FCSTD DOCUMENT  (FreeCAD 0.16R5097 (Git))
Label: Base section
License: All rights reserved
LicenseURL: http://en.wikipedia.org/wiki/All_rights_reserved
objects: Part::Part2DObjectPython×50, App::Annotation×8, App::FeaturePython×3, Part::Feature×1, App::DocumentObjectGroup×1
note: 51 computed .brp shape members not serialized (recipe doc carries the construction recipe); baked Part::Feature solids carry a one-line shape summary decoded from their .brp

FEATURE [Part::Part2DObjectPython] Rectangle  # Draft 2D object (typed FeaturePython)
  ChamferSize = 0
  FilletRadius = 0
  Height = 2438.4
  Length = 152.4
  MakeFace = true
  Placement = pos=(8.9e-11,-4058.4,0) rot=(0,0,1;0rad)
FEATURE [Part::Part2DObjectPython] Rectangle001  # Draft 2D object (typed FeaturePython)
  ChamferSize = 0
  FilletRadius = 0
  Height = 152.4
  Length = 4876.8
  MakeFace = true
  Placement = pos=(-152.4,-1680.96,0) rot=(0,0,1;0.197396rad)
  Support = -> Rectangle
FEATURE [Part::Part2DObjectPython] Rectangle002  # Draft 2D object (typed FeaturePython)
  ChamferSize = 0
  FilletRadius = 0
  Height = 152.4
  Length = 50.8
  MakeFace = true
  Placement = pos=(-152.4,-1680.96,0) rot=(0,0,1;0.197396rad)
FEATURE [Part::Part2DObjectPython] Rectangle003  # Draft 2D object (typed FeaturePython)
  ChamferSize = 0
  FilletRadius = 0
  Height = 152.4
  Length = 50.8
  MakeFace = true
  Placement = pos=(26.9286,-1541.48,0) rot=(0,0,1;1.76819rad)
FEATURE [Part::Part2DObjectPython] Rectangle004  # Draft 2D object (typed FeaturePython)
  ChamferSize = 0
  FilletRadius = 0
  Height = 152.4
  Length = 50.8
  MakeFace = true
  Placement = pos=(152.4,-1670.8,0) rot=(0,0,1;1.5708rad)
FEATURE [Part::Part2DObjectPython] Rectangle005  # Draft 2D object (typed FeaturePython)
  ChamferSize = 0
  FilletRadius = 0
  Height = 152.4
  Length = 50.8
  MakeFace = true
  Placement = pos=(152.4,-1670.8,0) rot=(0,0,1;3.14159rad)
FEATURE [Part::Part2DObjectPython] Rectangle006  # Draft 2D object (typed FeaturePython)
  ChamferSize = 0
  FilletRadius = 0
  Height = 152.4
  Length = 50.8
  MakeFace = true
  Placement = pos=(4579.88,-734.504,0) rot=(0,0,1;0.197396rad)
FEATURE [Part::Part2DObjectPython] Rectangle007  # Draft 2D object (typed FeaturePython)
  ChamferSize = 0
  FilletRadius = 0
  Height = 152.4
  Length = 50.8
  MakeFace = true
  Placement = pos=(4579.88,-734.504,0) rot=(0,0,1;1.76819rad)
FEATURE [Part::Part2DObjectPython] Rectangle008  # Draft 2D object (typed FeaturePython)
  ChamferSize = 0
  FilletRadius = 0
  Height = 152.4
  Length = 50.8
  MakeFace = true
  Placement = pos=(152.4,-4058.4,0) rot=(0,0,1;1.5708rad)
FEATURE [Part::Part2DObjectPython] Rectangle009  # Draft 2D object (typed FeaturePython)
  ChamferSize = 0
  FilletRadius = 0
  Height = 152.4
  Length = 50.8
  MakeFace = true
  Placement = pos=(152.4,-3855.2,0) rot=(0,0,1;3.14159rad)
FEATURE [Part::Part2DObjectPython] Rectangle010  # Draft 2D object (typed FeaturePython)
  ChamferSize = 0
  FilletRadius = 0
  Height = 5000
  Length = 522.38
  MakeFace = true
  Placement = pos=(4629.7,-4209.2,0) rot=(0,0,1;0rad)
FEATURE [Part::Part2DObjectPython] Line  # Draft 2D object (typed FeaturePython)
  ChamferSize = 0
  Closed = false
  End = (101.6,-1260.93,0)
  FilletRadius = 0
  Length = 647.743
  MakeFace = true
  Placement = pos=(-50.8,-1908.67,0) rot=(0,0,1;0rad)
  Points = (2) [(152.4,1.15278e-10,0),(152.4,647.743,0)]
  Start = (101.6,-1908.67,0)
FEATURE [Part::Part2DObjectPython] Line001  # Draft 2D object (typed FeaturePython)
  ChamferSize = 0
  Closed = false
  End = (50.8,-1260.93,0)
  FilletRadius = 0
  Length = 647.743
  MakeFace = true
  Placement = pos=(-101.6,-1908.67,0) rot=(0,0,1;0rad)
  Points = (2) [(152.4,1.15278e-10,0),(152.4,647.743,0)]
  Start = (50.8,-1908.67,0)
FEATURE [Part::Part2DObjectPython] Rectangle011  # Draft 2D object (typed FeaturePython)
  ChamferSize = 0
  FilletRadius = 0
  Height = 125
  Length = 12.7
  MakeFace = true
  Placement = pos=(-20.3985,-1667.51,0) rot=(0,0,1;1.76819rad)
FEATURE [Part::Part2DObjectPython] Rectangle012  # Draft 2D object (typed FeaturePython)
  ChamferSize = 0
  FilletRadius = 0
  Height = 152.4
  Length = 50.8
  MakeFace = true
  Placement = pos=(4629.7,-735.134,0) rot=(0,0,1;3.14159rad)
FEATURE [Part::Part2DObjectPython] Line002  # Draft 2D object (typed FeaturePython)
  ChamferSize = 0
  Closed = false
  End = (5428.22,-836.734,0)
  FilletRadius = 0
  Length = 1050.78
  MakeFace = true
  Placement = pos=(-92.5719,-1606.18,0) rot=(0,0,1;0rad)
  Points = (2) [(4470.01,769.444,0),(5520.79,769.444,0)]
  Start = (4377.44,-836.734,0)
FEATURE [Part::Part2DObjectPython] Line003  # Draft 2D object (typed FeaturePython)
  ChamferSize = 0
  Closed = false
  End = (5428.22,-785.934,0)
  FilletRadius = 0
  Length = 1050.78
  MakeFace = true
  Placement = pos=(-92.5719,-1555.38,0) rot=(0,0,1;0rad)
  Points = (2) [(4470.01,769.444,0),(5520.79,769.444,0)]
  Start = (4377.44,-785.934,0)
FEATURE [App::FeaturePython] Dimension  # Draft dimension (typed FeaturePython)
  Dimline = (3460.82,-387.376,0)
  Direction = (0,0,0)
  Distance = 4876.8
  End = (4599.81,-575.1,0)
  Normal = (0,0,1)
  Start = (-182.288,-1531.52,0)
FEATURE [Part::Part2DObjectPython] Rectangle013  # Draft 2D object (typed FeaturePython)
  ChamferSize = 0
  FilletRadius = 0
  Height = 100
  Length = 200
  MakeFace = true
  Placement = pos=(-23.8,-4209.2,0) rot=(0,0,1;0rad)
FEATURE [Part::Part2DObjectPython] Rectangle014  # Draft 2D object (typed FeaturePython)
  ChamferSize = 0
  FilletRadius = 0
  Height = -778.465
  Length = 723.456
  MakeFace = true
  Placement = pos=(-285.528,-4209.2,0) rot=(0,0,1;0rad)
FEATURE [Part::Part2DObjectPython] Rectangle015  # Draft 2D object (typed FeaturePython)
  ChamferSize = 0
  FilletRadius = 0
  Height = -778.465
  Length = 723.456
  MakeFace = true
  Placement = pos=(4529.16,-4209.2,0) rot=(0,0,1;0rad)
FEATURE [Part::Part2DObjectPython] Line004  # Draft 2D object (typed FeaturePython)
  ChamferSize = 0
  Closed = false
  End = (4529.16,-4209.2,0)
  FilletRadius = 0
  Length = 4091.23
  MakeFace = true
  Placement = pos=(0,-101.6,0) rot=(0,0,1;0rad)
  Points = (2) [(437.928,-4107.6,0),(4529.16,-4107.6,0)]
  Start = (437.928,-4209.2,0)
FEATURE [Part::Part2DObjectPython] Rectangle016  # Draft 2D object (typed FeaturePython)
  ChamferSize = 0
  FilletRadius = 0
  Height = 152.4
  Length = 50.8
  MakeFace = true
  Placement = pos=(152.4,-4109.2,0) rot=(0,0,1;1.5708rad)
FEATURE [Part::Part2DObjectPython] Line005  # Draft 2D object (typed FeaturePython)
  ChamferSize = 0
  Closed = false
  End = (76.2,-3764.74,0)
  FilletRadius = 0
  Length = 647.743
  MakeFace = true
  Placement = pos=(-76.2,-4412.49,0) rot=(0,0,1;0rad)
  Points = (2) [(152.4,1.15278e-10,0),(152.4,647.743,0)]
  Start = (76.2,-4412.49,0)
FEATURE [Part::Feature] Polyline  label="Person"
  Placement = pos=(2144.04,-4210.4,0) rot=(0,0,1;0rad)
  shape: bbox 1200 x 1818 x 2e-07 mm, 0 faces, 0 solids (baked)
FEATURE [App::FeaturePython] Dimension001  # Draft dimension (typed FeaturePython)
  Dimline = (-514.519,-2392.01,0)
  Direction = (0,0,0)
  Distance = 2438.4
  End = (8.9e-11,-1620,0)
  Normal = (0,0,1)
  Start = (8.9e-11,-4058.4,0)
FEATURE [App::Annotation] Text
  LabelText = 16' Roof panel | 20% slope
  Position = (-2666.11,-30.1774,0)
FEATURE [Part::Part2DObjectPython] DWire  # Draft 2D object (typed FeaturePython)
  ChamferSize = 0
  Closed = false
  End = (-1566.37,17.1876,0)
  FilletRadius = 0
  Length = 3282.33
  MakeFace = true
  Placement = pos=(0,-400.8,0) rot=(0,0,1;0rad)
  Points = (3) [(1362.29,-901.705,0),(-923.076,417.988,0),(-1566.37,417.988,0)]
  Start = (1362.29,-1302.5,0)
FEATURE [App::Annotation] Text001
  LabelText = 8' Wall panel
  Position = (-2497.25,-2807.56,0)
FEATURE [Part::Part2DObjectPython] Line006  # Draft 2D object (typed FeaturePython)
  ChamferSize = 0
  Closed = false
  End = (-1581.02,-2769.61,0)
  FilletRadius = 0
  Length = 1658.15
  MakeFace = true
  Points = (2) [(77.136,-2769.61,0),(-1581.02,-2769.61,0)]
  Start = (77.136,-2769.61,0)
FEATURE [App::Annotation] Text002
  LabelText = Base lumber fixed to wall
  Position = (-2517.74,-3766.66,0)
FEATURE [Part::Part2DObjectPython] DWire001  # Draft 2D object (typed FeaturePython)
  ChamferSize = 0
  Closed = false
  End = (-826.195,-3718.63,0)
  FilletRadius = 0
  Length = 962.724
  MakeFace = true
  Placement = pos=(0,-400.8,0) rot=(0,0,1;0rad)
  Points = (3) [(40.5394,-3686.9,-3.63798e-12),(-620.962,-3317.83,0),(-826.195,-3317.83,0)]
  Start = (40.5394,-4087.7,-4e-12)
FEATURE [App::Annotation] Text004
  LabelText = Brick wall
  Position = (-2518.73,-4197.79,0)
FEATURE [Part::Part2DObjectPython] Line008  # Draft 2D object (typed FeaturePython)
  ChamferSize = 0
  Closed = false
  End = (-1752.02,-4159.49,0)
  FilletRadius = 0
  Length = 1796.36
  MakeFace = true
  Placement = pos=(0,-121.402,0) rot=(0,0,1;0rad)
  Points = (2) [(44.3355,-4038.09,0),(-1752.02,-4038.09,0)]
  Start = (44.3355,-4159.49,0)
FEATURE [App::Annotation] Text005
  LabelText = Dent in roof panel
  Position = (-2571.01,-1065.68,0)
FEATURE [Part::Part2DObjectPython] DWire002  # Draft 2D object (typed FeaturePython)
  ChamferSize = 0
  Closed = false
  End = (-1335.08,-1042.56,0)
  FilletRadius = 0
  Length = 1571.43
  MakeFace = true
  Placement = pos=(0,-400.8,0) rot=(0,0,1;0rad)
  Points = (3) [(71.6956,-1211.56,0),(-831.87,-641.759,0),(-1335.08,-641.759,0)]
  Start = (71.6956,-1612.36,0)
FEATURE [App::Annotation] Text006
  LabelText = Finishing board
  Position = (-2546.96,-2098.36,0)
FEATURE [Part::Part2DObjectPython] DWire003  # Draft 2D object (typed FeaturePython)
  ChamferSize = 0
  Closed = false
  End = (-1462.47,-2094.45,0)
  FilletRadius = 0
  Length = 1481.11
  MakeFace = true
  Placement = pos=(0,-400.8,0) rot=(0,0,1;0rad)
  Points = (3) [(-60.1521,-1322.04,0),(-897.069,-1693.65,0),(-1462.47,-1693.65,0)]
  Start = (-60.1521,-1722.84,0)
FEATURE [Part::Part2DObjectPython] DWire004  # Draft 2D object (typed FeaturePython)
  ChamferSize = 0
  Closed = true
  End = (8.9e-11,-1249.68,0)
  FilletRadius = 0
  Length = 10085.9
  MakeFace = true
  Points = (7) [(-152.4,-1280.16,0),(-182.288,-1130.72,0),(4599.81,-174.3,0),(4629.7,-323.741,0),(152.4,-1219.2,0),(8.90452e-11,-1219.2,0),(8.90282e-11,-1249.68,0)]
  Start = (-152.4,-1280.16,0)
FEATURE [Part::Part2DObjectPython] Rectangle018  # Draft 2D object (typed FeaturePython)
  ChamferSize = 0
  FilletRadius = 0
  Height = 11.1125
  Length = 4876.8
  MakeFace = true
  Placement = pos=(-182.288,-1531.52,0) rot=(0,0,1;0.197396rad)
FEATURE [Part::Part2DObjectPython] Rectangle019  # Draft 2D object (typed FeaturePython)
  ChamferSize = 0
  FilletRadius = 0
  Height = 2438.4
  Length = 11.1125
  MakeFace = true
  Placement = pos=(-11.1125,-4058.4,0) rot=(0,0,1;0rad)
FEATURE [Part::Part2DObjectPython] DWire005  # Draft 2D object (typed FeaturePython)
  ChamferSize = 0
  Closed = false
  End = (-161.67,-1541.05,0)
  FilletRadius = 0
  Length = 87.7772
  MakeFace = true
  Placement = pos=(0,-400.8,0) rot=(0,0,1;0rad)
  Points = (4) [(-171.767,-1106.66,0),(-195.649,-1111.32,0),(-189.436,-1145.88,0),(-161.67,-1140.25,0)]
  Start = (-171.767,-1507.46,0)
FEATURE [Part::Part2DObjectPython] DWire006  # Draft 2D object (typed FeaturePython)
  ChamferSize = 0
  Closed = false
  End = (-34.7813,-1631.15,0)
  FilletRadius = 0
  Length = 68.1851
  MakeFace = true
  Placement = pos=(0,-400.8,0) rot=(0,0,1;0rad)
  Points = (3) [(-15.5742,-1279.33,0),(-15.5742,-1230.35,0),(-34.7813,-1230.35,0)]
  Start = (-15.5742,-1680.13,0)
FEATURE [Part::Part2DObjectPython] DWire007  # Draft 2D object (typed FeaturePython)
  ChamferSize = 0
  Closed = false
  End = (4595.7,-348.454,0)
  FilletRadius = 0
  Length = 332.263
  MakeFace = true
  Placement = pos=(0,-400.8,0) rot=(0,0,1;0rad)
  Points = (3) [(4450.38,-162.586,0),(4595.7,-131.26,0),(4595.7,52.3464,0)]
  Start = (4450.38,-563.386,0)
FEATURE [Part::Part2DObjectPython] Line009  # Draft 2D object (typed FeaturePython)
  ChamferSize = 0
  Closed = false
  End = (4807.89,-446.588,0)
  FilletRadius = 0
  Length = 291.238
  MakeFace = true
  Placement = pos=(0,-400.8,0) rot=(0,0,1;0rad)
  Points = (2) [(4516.66,-45.7882,0),(4807.89,-45.7882,0)]
  Start = (4516.66,-446.588,0)
FEATURE [App::Annotation] Text007
  LabelText = Flashing
  Position = (2432.2,257.338,0)
FEATURE [Part::Part2DObjectPython] DWire008  # Draft 2D object (typed FeaturePython)
  ChamferSize = 0
  Closed = false
  End = (3052.14,288.618,0)
  FilletRadius = 0
  Length = 1750.97
  MakeFace = true
  Placement = pos=(0,-400.8,0) rot=(0,0,1;0rad)
  Points = (3) [(4554.15,-95.885,0),(3440.06,689.418,0),(3052.14,689.418,0)]
  Start = (4554.15,-496.685,0)
FEATURE [Part::Part2DObjectPython] Circle  # Draft 2D object (typed FeaturePython)
  FirstAngle = 0
  LastAngle = 0
  MakeFace = true
  Placement = pos=(76.1173,-4055.83,0) rot=(0,1,0;3.14159rad)
  Radius = 331.844
FEATURE [Part::Part2DObjectPython] Circle001  # Draft 2D object (typed FeaturePython)
  FirstAngle = 0
  LastAngle = 0
  MakeFace = true
  Placement = pos=(8.9e-11,-1650.48,0) rot=(0,0,1;0rad)
  Radius = 358.624
FEATURE [Part::Part2DObjectPython] Circle002  # Draft 2D object (typed FeaturePython)
  FirstAngle = 0
  LastAngle = 0
  MakeFace = true
  Placement = pos=(4629.7,-724.541,0) rot=(0,0,1;0rad)
  Radius = 463.13
FEATURE [Part::Part2DObjectPython] Rectangle020  # Draft 2D object (typed FeaturePython)
  ChamferSize = 0
  FilletRadius = 0
  Height = 152.4
  Length = 50.8
  MakeFace = true
  Placement = pos=(4578.9,-748.114,0) rot=(0,0,1;3.14159rad)
FEATURE [Part::Part2DObjectPython] Line011  # Draft 2D object (typed FeaturePython)
  ChamferSize = 0
  Closed = false
  End = (4619.47,-1133.79,0)
  FilletRadius = 0
  Length = 756.941
  MakeFace = true
  Placement = pos=(1239.31,-159.34,0) rot=(0,0,1;0rad)
  Points = (2) [(3231.71,-232.207,0),(3380.16,-974.448,0)]
  Start = (4471.02,-391.547,0)
FEATURE [Part::Part2DObjectPython] DWire009  # Draft 2D object (typed FeaturePython)
  ChamferSize = 0
  Closed = false
  End = (-33.5428,-4124.98,0)
  FilletRadius = 0
  Length = 268.403
  MakeFace = true
  Points = (4) [(186.183,-4123.64,0),(186.183,-4099.97,0),(-33.5428,-4099.97,0),(-33.5428,-4124.98,0)]
  Start = (186.183,-4123.64,0)
FEATURE [App::Annotation] Text008
  LabelText = Flashing
  Position = (-2516.03,-3991.32,0)
FEATURE [Part::Part2DObjectPython] DWire010  # Draft 2D object (typed FeaturePython)
  ChamferSize = 0
  Closed = false
  End = (-1898.25,-3978.59,0)
  FilletRadius = 0
  Length = 1882.13
  MakeFace = true
  Points = (3) [(-50.282,-4110.41,0),(-287.507,-3978.59,0),(-1898.25,-3978.59,0)]
  Start = (-50.282,-4110.41,0)
FEATURE [App::DocumentObjectGroup] Group  label="Section"
  Group = -> [Rectangle,Rectangle001,Rectangle002,Rectangle003,Rectangle004,Rectangle005,Rectangle006,Rectangle007,Rectangle008,Rectangle009,Rectangle010,Line,Line001,Rectangle011,Rectangle012,Line002,Line003,Dimension,Rectangle013,Rectangle014,Rectangle015,Line004,Rectangle016,Line005,Polyline,Dimension001,Text,DWire,Text001,Line006,Text002,DWire001,Text004,Line008,Text005,DWire002,Text006,DWire003,DWire004,+16 more]
FEATURE [App::FeaturePython] Dimension002  # Draft dimension (typed FeaturePython)
  Dimline = (700.265,-2646.59,0)
  Direction = (0,0,0)
  Distance = 2589.31
  End = (152.4,-1620,0)
  Normal = (0,0,1)
  Start = (176.2,-4209.2,0)
FEATURE [Part::Part2DObjectPython] Rectangle021  # Draft 2D object (typed FeaturePython)
  ChamferSize = 0
  FilletRadius = 0
  Height = 2438.4
  Length = 1219.2
  MakeFace = false
  Placement = pos=(152.4,-4058.4,0) rot=(0,0,1;0rad)
FEATURE [Part::Part2DObjectPython] Rectangle022  # Draft 2D object (typed FeaturePython)
  ChamferSize = 0
  FilletRadius = 0
  Height = 2438.4
  Length = 1219.2
  MakeFace = false
  Placement = pos=(1371.6,-4058.4,0) rot=(0,0,1;0rad)
FEATURE [Part::Part2DObjectPython] Rectangle023  # Draft 2D object (typed FeaturePython)
  ChamferSize = 0
  FilletRadius = 0
  Height = 2438.4
  Length = 1219.2
  MakeFace = false
  Placement = pos=(2590.8,-4058.4,0) rot=(0,0,1;0rad)
FEATURE [Part::Part2DObjectPython] Rectangle024  # Draft 2D object (typed FeaturePython)
  ChamferSize = 0
  FilletRadius = 0
  Height = 2438.4
  Length = 820
  MakeFace = false
  Placement = pos=(3810,-4058.4,0) rot=(0,0,1;0rad)
FEATURE [Part::Part2DObjectPython] Line012  # Draft 2D object (typed FeaturePython)
  ChamferSize = 0
  Closed = false
  End = (282.609,-1747,0)
  FilletRadius = 0
  Length = 263.855
  MakeFace = true
  Placement = pos=(0,-2.65601,0) rot=(0,0,1;0rad)
  Points = (2) [(18.754,-1744.34,0),(282.609,-1744.34,0)]
  Start = (18.754,-1747,0)
FEATURE [Part::Part2DObjectPython] Line013  # Draft 2D object (typed FeaturePython)
  ChamferSize = 0
  Closed = false
  End = (282.609,-3931.4,0)
  FilletRadius = 0
  Length = 263.855
  MakeFace = true
  Placement = pos=(0,-2187.06,0) rot=(0,0,1;0rad)
  Points = (2) [(18.754,-1744.34,0),(282.609,-1744.34,0)]
  Start = (18.754,-3931.4,0)
